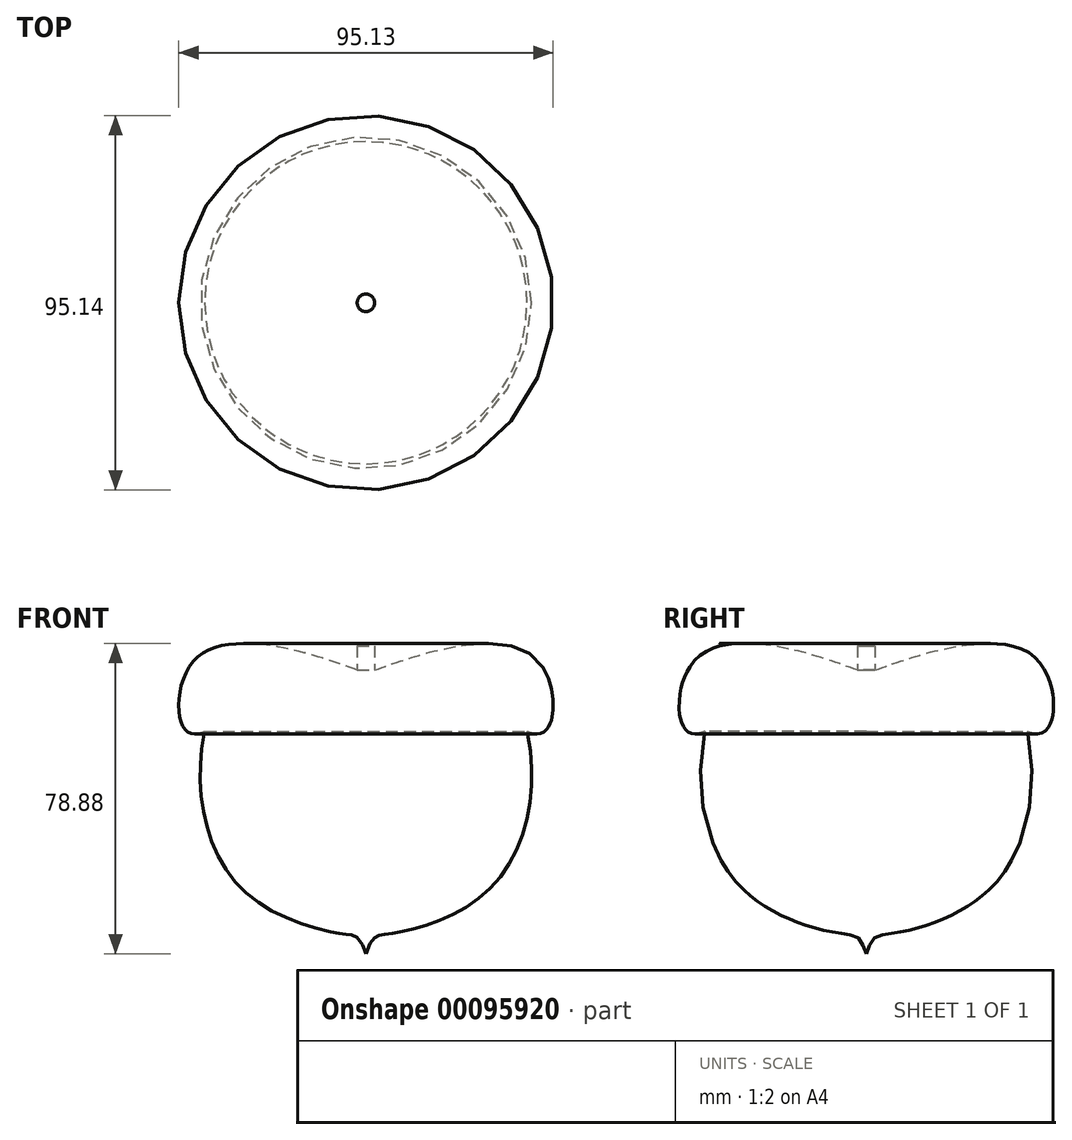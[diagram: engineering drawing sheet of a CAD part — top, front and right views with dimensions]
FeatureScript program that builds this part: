
annotation { "Feature Type Name" : "Feature", "Feature Type Description" : "" }
export const myFeature = defineFeature(function(context is Context, id is Id, definition is map)
    precondition{}
    {
        {
            var Q0;
            Q0=qCreatedBy(makeId("Front.planeOp"),FACE);
            var sketch = newSketch(context, id + "F0", { "sketchPlane" : qUnion([Q0])});
            skLineSegment(sketch, "E0", {"start": v(0, 0) * mm, "end": v(0, 56.59) * mm});
            skLineSegment(sketch, "E1", {"start": v(0, 56.59) * mm, "end": v(40.93, 56.59) * mm});
            skFitSpline(sketch, "E2", {"points": [v(40.93, 56.59) * mm, v(31.07, 16.15) * mm, v(5.42, 5.05) * mm, v(0, 0) * mm], "startDerivative": vector(21.55, -101.13) * mm, "endDerivative": vector(-27.5, -80.53) * mm});
            skSolve(sketch);
        }
        {
            var Q0;
            Q0=makeQuery(id+"F0.imprint","IMPRINT",FACE,{"disambiguationData":[TD([[makeQuery(id+"F0.imprint","IMPRINT",EDGE,{"derivedFrom":sQuery(id+"F0.wireOp",EDGE,"E0")}),-1.0]])]});
            var Q1;
            Q1=sQuery(id+"F0.wireOp",EDGE,"E0");
            revolve(context, id + "F1", {"entities" : qUnion([Q0]), "axis" : qUnion([Q1]), "revolveType" : RevolveType.FULL});
        }
        {
            var Q0;
            Q0=qCreatedBy(makeId("Front.planeOp"),FACE);
            var sketch = newSketch(context, id + "F2", { "sketchPlane" : qUnion([Q0])});
            skLineSegment(sketch, "E3.0", {"start": v(40.93, 56.59) * mm, "end": v(-40.93, 56.59) * mm});
            skLineSegment(sketch, "E4", {"start": v(0, 56.59) * mm, "end": v(0, 78.28) * mm});
            skLineSegment(sketch, "E5", {"start": v(0, 78.28) * mm, "end": v(2.22, 78.28) * mm});
            skLineSegment(sketch, "E6", {"start": v(2.22, 78.28) * mm, "end": v(2.22, 72.12) * mm});
            skFitSpline(sketch, "E7", {"points": [v(2.22, 72.12) * mm, v(19.97, 77.54) * mm, v(42.9, 75.33) * mm, v(46.85, 58.56) * mm, v(40.93, 56.59) * mm], "startDerivative": vector(62.5, 21.74) * mm, "endDerivative": vector(-56.89, 24.94) * mm});
            skSolve(sketch);
        }
        {
            var Q0;
            {var subQ0=sQuery(id+"F2.wireOp",EDGE,"E4");Q0=makeQuery(id+"F2.imprint","IMPRINT",FACE,{"disambiguationData":[TD([[makeQuery(id+"F2.imprint","IMPRINT",EDGE,{"derivedFrom":subQ0}),-1.0]])]});}
            var Q1;
            Q1=sQuery(id+"F2.wireOp",EDGE,"E4");
            revolve(context, id + "F3", {"operationType" : NewBodyOperationType.ADD, "entities" : qUnion([Q0]), "axis" : qUnion([Q1]), "revolveType" : RevolveType.FULL});
        }
    });
